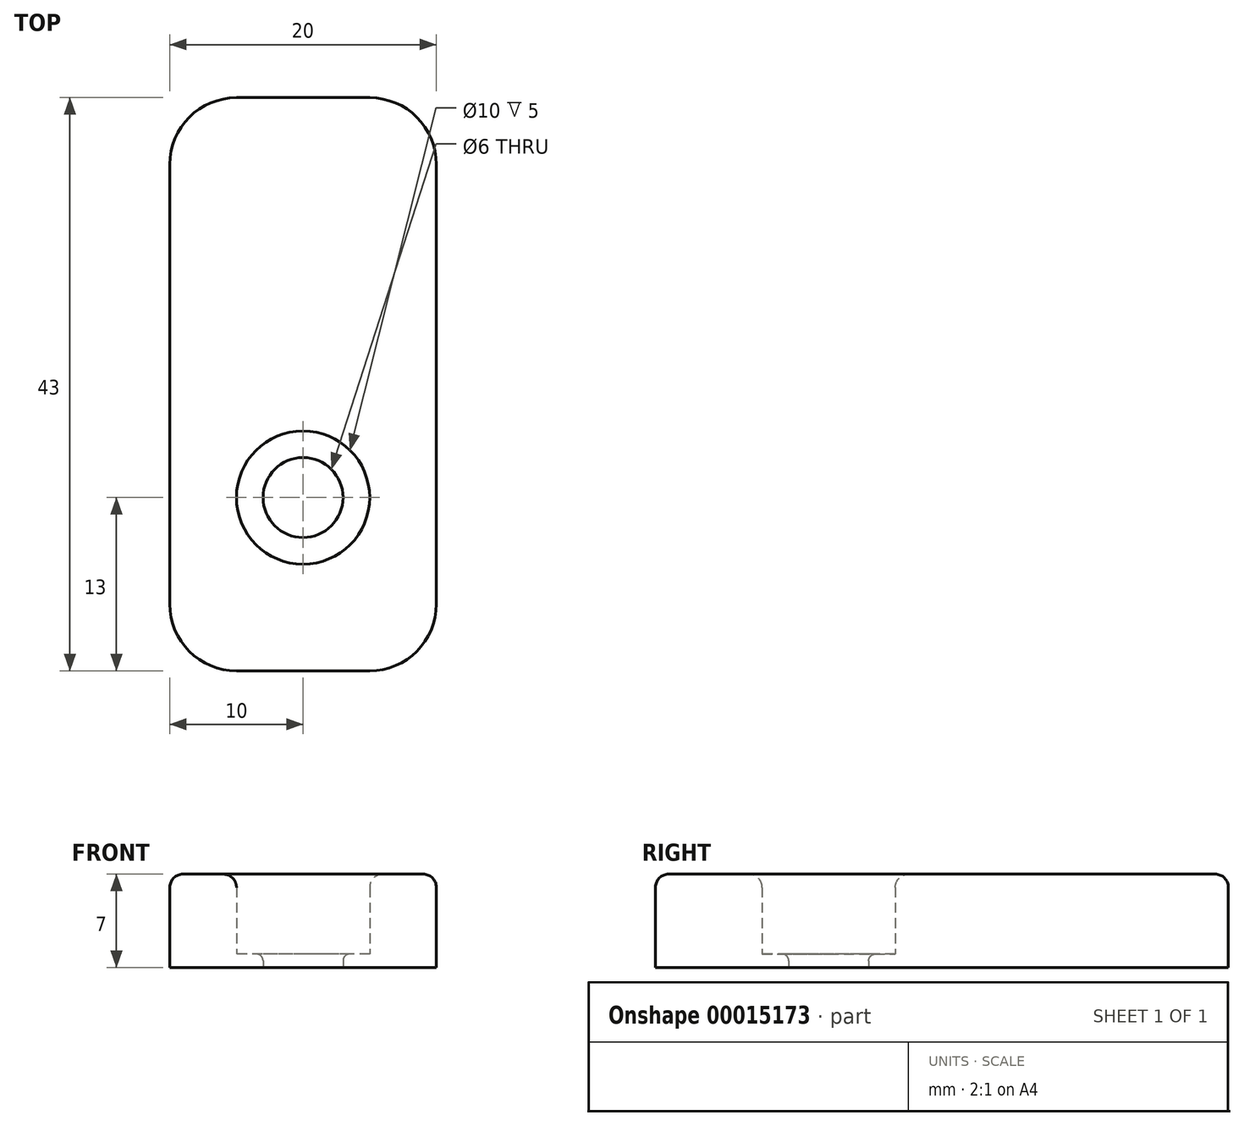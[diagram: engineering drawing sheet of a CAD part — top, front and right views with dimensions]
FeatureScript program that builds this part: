
annotation { "Feature Type Name" : "Feature", "Feature Type Description" : "" }
export const myFeature = defineFeature(function(context is Context, id is Id, definition is map)
    precondition{}
    {
        {
            var Q0;
            Q0=qCreatedBy(makeId("Top.planeOp"),FACE);
            var sketch = newSketch(context, id + "F0", { "sketchPlane" : qUnion([Q0])});
            skCircle(sketch, "E0", {"center": v(0, 0) * mm, "radius": 3 * mm});
            skCircle(sketch, "E1", {"center": v(0, 0) * mm, "radius": 5 * mm});
            skLineSegment(sketch, "E2.bottom", {"start": v(-10, -13) * mm, "end": v(10, -13) * mm});
            skLineSegment(sketch, "E2.top", {"start": v(-10, 30) * mm, "end": v(10, 30) * mm});
            skLineSegment(sketch, "E2.left", {"start": v(-10, -13) * mm, "end": v(-10, 30) * mm});
            skLineSegment(sketch, "E2.right", {"start": v(10, -13) * mm, "end": v(10, 30) * mm});
            skLineSegment(sketch, "E3", {"start": v(0, -13) * mm, "end": v(0, 0) * mm, "construction": true});
            skLineSegment(sketch, "E4", {"start": v(-10, 10) * mm, "end": v(10, 10) * mm});
            skSolve(sketch);
        }
        {
            var Q0;
            Q0=makeQuery(id+"F0.imprint","IMPRINT",FACE,{"disambiguationData":[TD([[makeQuery(id+"F0.imprint","IMPRINT",EDGE,{"derivedFrom":sQuery(id+"F0.wireOp",EDGE,"E1")}),-1.0]])]});
            extrude(context, id + "F1", {"entities" : qUnion([Q0]), "depth" : 7 * mm});
        }
        {
            var Q0;
            Q0=makeQuery(id+"F0.imprint","IMPRINT",FACE,{"disambiguationData":[TD([[makeQuery(id+"F0.imprint","IMPRINT",EDGE,{"derivedFrom":sQuery(id+"F0.wireOp",EDGE,"E0")}),-1.0]])]});
            extrude(context, id + "F2", {"entities" : qUnion([Q0]), "operationType" : NewBodyOperationType.ADD, "depth" : 1 * mm});
        }
        {
            var Q0;
            Q0=makeQuery(id+"F1.opExtrude","SWEPT_FACE",FACE,{"disambiguationData":[OSD([sQuery(id+"F0.wireOp",EDGE,"E2.right")])]});
            var sketch = newSketch(context, id + "F3", { "sketchPlane" : qUnion([Q0])});
            skLineSegment(sketch, "E5", {"start": v(10, 7) * mm, "end": v(30, 7) * mm});
            skLineSegment(sketch, "E6.0", {"start": v(-13, 0) * mm, "end": v(30, 0) * mm});
            skLineSegment(sketch, "E7", {"start": v(30, 0) * mm, "end": v(30, 7) * mm});
            skSolve(sketch);
        }
        {
            var Q0;
            Q0=makeQuery(id+"F1.opExtrude","SWEPT_FACE",FACE,{"disambiguationData":[OSD([sQuery(id+"F0.wireOp",EDGE,"E2.left")])]});
            cPlane(context, id + "F4", {"entities" : qUnion([Q0]), "cplaneType" : CPlaneType.OFFSET, "offset" : 0 * mm, "width" : 150 * mm, "height" : 150 * mm});
        }
        {
            var Q0;
            Q0=makeQuery(id+"F3.imprint","IMPRINT",FACE,{"disambiguationData":[TD([[makeQuery(id+"F3.imprint","IMPRINT",EDGE,{"derivedFrom":sQuery(id+"F3.wireOp",EDGE,"E5")}),-1.0]])]});
            var Q1;
            Q1=qCreatedBy(id+"F4.planeOp",FACE);
            extrude(context, id + "F5", {"entities" : qUnion([Q0]), "operationType" : NewBodyOperationType.ADD, "endBound" : BoundingType.UP_TO_SURFACE, "oppositeDirection" : true, "endBoundEntityFace" : qUnion([Q1]), "depth" : 25 * mm});
        }
        {
            var Q0;
            Q0=makeQuery(id+"F1.opExtrude","SWEPT_EDGE",EDGE,{"disambiguationData":[OSD([sQuery(id+"F0.wireOp",EDGE,"E2.bottom"),sQuery(id+"F0.wireOp",EDGE,"E2.right")])]});
            var Q1;
            Q1=makeQuery(id+"F1.opExtrude","SWEPT_EDGE",EDGE,{"disambiguationData":[OSD([sQuery(id+"F0.wireOp",EDGE,"E2.bottom"),sQuery(id+"F0.wireOp",EDGE,"E2.left")])]});
            var Q2;
            Q2=makeQuery(id+"F5.opExtrude","CAP_EDGE",EDGE,{"disambiguationData":[OSD([sQuery(id+"F3.wireOp",EDGE,"E7")])],"isStart":true});
            var Q3;
            Q3=makeQuery(id+"F5.opExtrude","CAP_EDGE",EDGE,{"disambiguationData":[OSD([sQuery(id+"F3.wireOp",EDGE,"E7")])],"isStart":false});
            fillet(context, id + "F6", {"entities" : qUnion([Q0, Q1, Q2, Q3]), "radius" : 5 * mm, "tangentPropagation" : true, "allowEdgeOverflow" : false});
        }
        {
            var Q0;
            Q0=makeQuery(id+"F5.opExtrude","SWEPT_EDGE",EDGE,{"disambiguationData":[OSD([sQuery(id+"F3.wireOp",EDGE,"E5"),sQuery(id+"F3.wireOp",EDGE,"E7")])]});
            var Q1;
            Q1=makeQuery(id+"F1.opExtrude","CAP_EDGE",EDGE,{"disambiguationData":[OSD([sQuery(id+"F0.wireOp",EDGE,"E2.bottom")])],"isStart":false});
            fillet(context, id + "F7", {"entities" : qUnion([Q0, Q1]), "radius" : 1 * mm, "tangentPropagation" : true, "allowEdgeOverflow" : false});
        }
        {
            var Q0;
            Q0=makeQuery(id+"F1.opExtrude","CAP_EDGE",EDGE,{"disambiguationData":[OSD([sQuery(id+"F0.wireOp",EDGE,"E1")])],"isStart":false});
            fillet(context, id + "F8", {"entities" : qUnion([Q0]), "radius" : 1 * mm, "tangentPropagation" : true, "allowEdgeOverflow" : false});
        }
        {
            var Q0;
            Q0=makeQuery(id+"F2.opExtrude","CAP_EDGE",EDGE,{"disambiguationData":[OSD([sQuery(id+"F0.wireOp",EDGE,"E1")])],"isStart":false});
            var Q1;
            Q1=makeQuery(id+"F2.opExtrude","CAP_EDGE",EDGE,{"disambiguationData":[OSD([sQuery(id+"F0.wireOp",EDGE,"E0")])],"isStart":false});
            fillet(context, id + "F9", {"entities" : qUnion([Q0, Q1]), "radius" : 0.5 * mm, "tangentPropagation" : true, "allowEdgeOverflow" : false});
        }
    });
